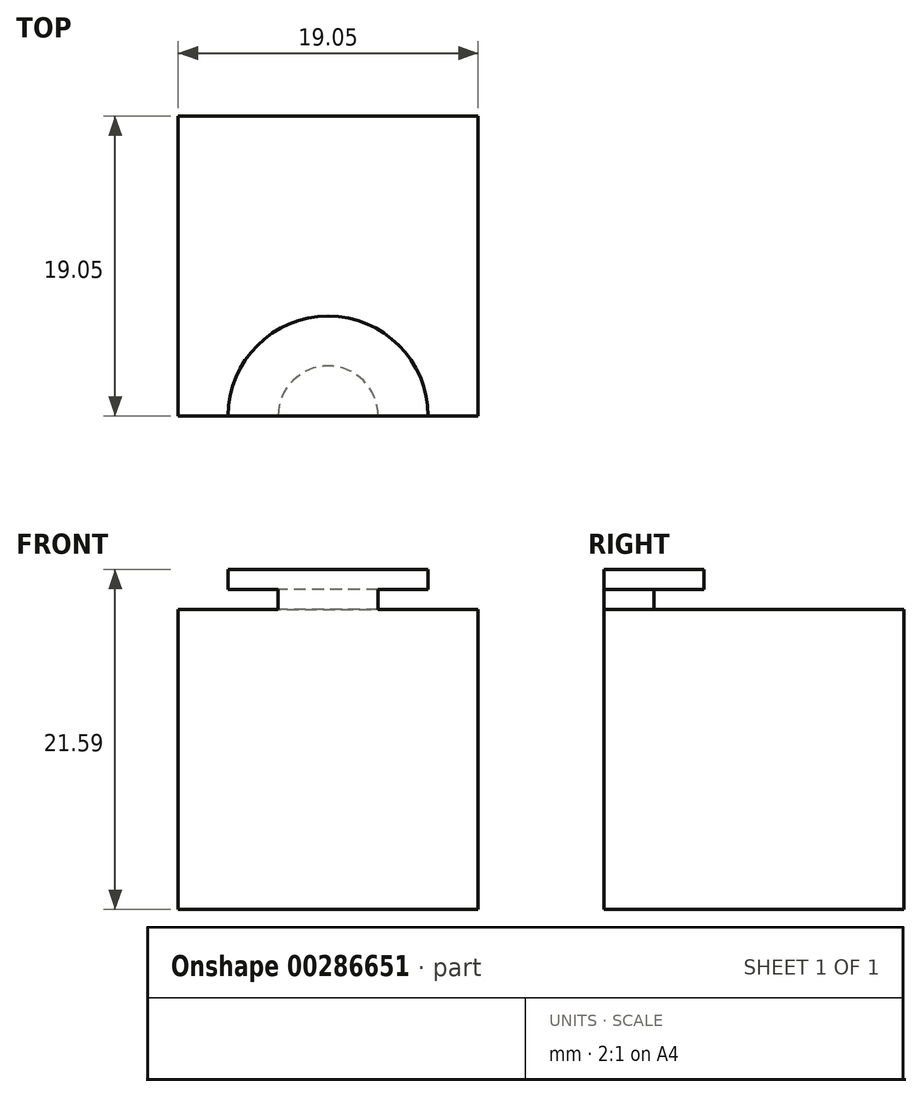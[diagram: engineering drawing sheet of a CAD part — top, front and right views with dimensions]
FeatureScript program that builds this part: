
annotation { "Feature Type Name" : "Feature", "Feature Type Description" : "" }
export const myFeature = defineFeature(function(context is Context, id is Id, definition is map)
    precondition{}
    {
        {
            var Q0;
            Q0=qCreatedBy(makeId("Front.planeOp"),FACE);
            var sketch = newSketch(context, id + "F0", { "sketchPlane" : qUnion([Q0])});
            skLineSegment(sketch, "E0.bottom", {"start": v(-51.85, 53.54) * mm, "end": v(-32.8, 53.54) * mm});
            skLineSegment(sketch, "E0.top", {"start": v(-51.85, 34.49) * mm, "end": v(-32.8, 34.49) * mm});
            skLineSegment(sketch, "E0.left", {"start": v(-51.85, 53.54) * mm, "end": v(-51.85, 34.49) * mm});
            skLineSegment(sketch, "E0.right", {"start": v(-32.8, 53.54) * mm, "end": v(-32.8, 34.49) * mm});
            skSolve(sketch);
        }
        {
            var Q0;
            Q0 = qSketchRegion(id + "F0", true);
            extrude(context, id + "F1", {"entities" : qUnion([Q0]), "depth" : 19.05 * mm});
        }
        {
            var Q0;
            Q0=makeQuery(id+"F1.opExtrude","SWEPT_FACE",FACE,{"disambiguationData":[OSD([sQuery(id+"F0.wireOp",EDGE,"E0.bottom")])]});
            var sketch = newSketch(context, id + "F2", { "sketchPlane" : qUnion([Q0])});
            skArc(sketch, "E1", {"start": v(-39.15, -19.05) * mm, "mid": v(-42.33, -15.88) * mm, "end": v(-45.5, -19.05) * mm});
            skSolve(sketch);
        }
        {
            var Q0;
            Q0 = qSketchRegion(id + "F2", true);
            var Q1;
            {var subQ0=sQuery(id+"F2.wireOp",EDGE,"E1");Q1=makeQuery(id+"F2.imprint","IMPRINT",FACE,{"disambiguationData":[TD([[makeQuery(id+"F2.imprint","IMPRINT",EDGE,{"derivedFrom":subQ0}),1.0]])]});}
            extrude(context, id + "F3", {"entities" : qUnion([Q0, Q1]), "operationType" : NewBodyOperationType.ADD, "depth" : 1.27 * mm});
        }
        {
            var Q0;
            Q0=makeQuery(id+"F3.opExtrude","CAP_FACE",FACE,{"disambiguationData":[OSD([sQuery(id+"F0.wireOp",EDGE,"E0.bottom"),sQuery(id+"F2.wireOp",EDGE,"E1")])],"isStart":false});
            var sketch = newSketch(context, id + "F4", { "sketchPlane" : qUnion([Q0])});
            skArc(sketch, "E2", {"start": v(-35.98, -19.05) * mm, "mid": v(-42.33, -12.7) * mm, "end": v(-48.68, -19.05) * mm});
            skLineSegment(sketch, "E3", {"start": v(-35.98, -19.05) * mm, "end": v(-48.68, -19.05) * mm});
            skSolve(sketch);
        }
        {
            var Q0;
            {var subQ1=makeQuery(id+"F3.opExtrude","CAP_EDGE",EDGE,{"disambiguationData":[OSD([sQuery(id+"F2.wireOp",EDGE,"E1")])],"isStart":false});Q0=makeQuery(id+"F4.imprint","IMPRINT",FACE,{"disambiguationData":[TD([[makeQuery(id+"F4.imprint","IMPRINT",EDGE,{"derivedFrom":subQ1}),1.0]])]});}
            var Q1;
            {var subQ0=sQuery(id+"F4.wireOp",EDGE,"E2");Q1=makeQuery(id+"F4.imprint","IMPRINT",FACE,{"disambiguationData":[TD([[makeQuery(id+"F4.imprint","IMPRINT",EDGE,{"derivedFrom":subQ0}),1.0]])]});}
            extrude(context, id + "F5", {"entities" : qUnion([Q0, Q1]), "operationType" : NewBodyOperationType.ADD, "depth" : 1.27 * mm});
        }
    });
